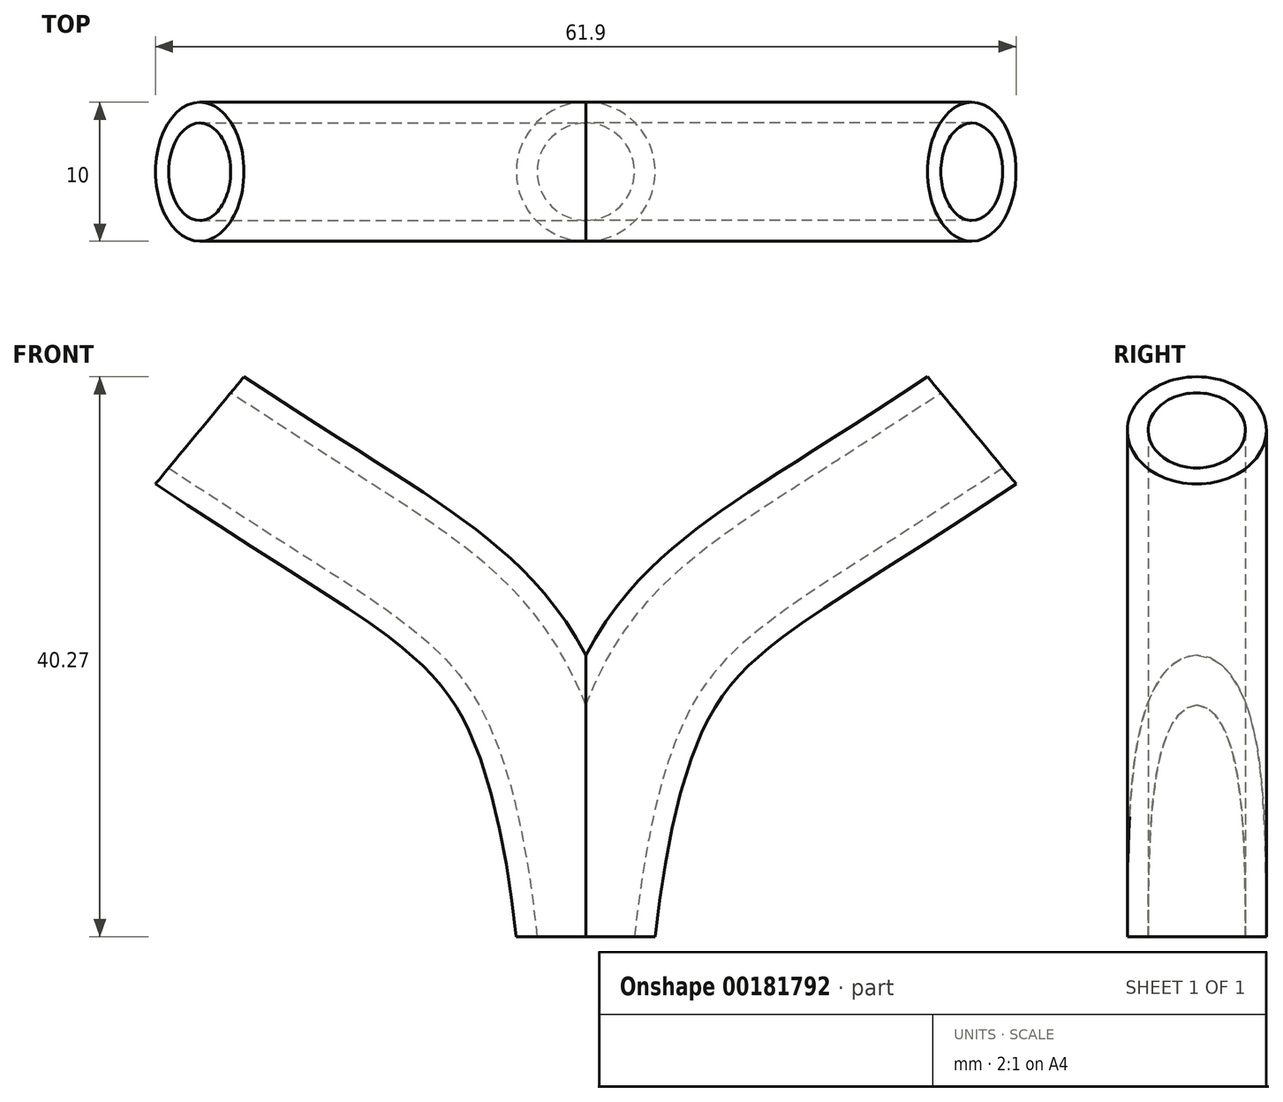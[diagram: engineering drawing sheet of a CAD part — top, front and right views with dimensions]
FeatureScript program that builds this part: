
annotation { "Feature Type Name" : "Feature", "Feature Type Description" : "" }
export const myFeature = defineFeature(function(context is Context, id is Id, definition is map)
    precondition{}
    {
        {
            var Q0;
            Q0=qCreatedBy(makeId("Front.planeOp"),FACE);
            var sketch = newSketch(context, id + "F0", { "sketchPlane" : qUnion([Q0])});
            skFitSpline(sketch, "E0", {"points": [v(0, 0) * mm, v(-8.85, 23.6) * mm, v(-27.77, 36.41) * mm], "startDerivative": vector(-9.3, 88.24) * mm, "endDerivative": vector(-66.03, 43.73) * mm});
            skSolve(sketch);
        }
        {
            var Q0;
            Q0=qCreatedBy(makeId("Top.planeOp"),FACE);
            var sketch = newSketch(context, id + "F1", { "sketchPlane" : qUnion([Q0])});
            skCircle(sketch, "E1", {"center": v(0, 0) * mm, "radius": 5 * mm});
            skCircle(sketch, "E2.0", {"center": v(0, 0) * mm, "radius": 3.5 * mm});
            skSolve(sketch);
        }
        {
            var Q0;
            Q0=makeQuery(id+"F1.imprint","IMPRINT",FACE,{"disambiguationData":[TD([[makeQuery(id+"F1.imprint","IMPRINT",EDGE,{"derivedFrom":sQuery(id+"F1.wireOp",EDGE,"E1")}),1.0]])]});
            var Q1;
            Q1=sQuery(id+"F0.wireOp",EDGE,"E0");
            sweep(context, id + "F2", {"profiles" : qUnion([Q0]), "path" : qUnion([Q1])});
        }
        {
            var Q0;
            Q0=qCreatedBy(makeId("Right.planeOp"),FACE);
            var sketch = newSketch(context, id + "F3", { "sketchPlane" : qUnion([Q0])});
            skLineSegment(sketch, "E3.bottom", {"start": v(-20.21, 23.68) * mm, "end": v(25, 23.68) * mm});
            skLineSegment(sketch, "E3.top", {"start": v(-20.21, -8.66) * mm, "end": v(25, -8.66) * mm});
            skLineSegment(sketch, "E3.left", {"start": v(-20.21, 23.68) * mm, "end": v(-20.21, -8.66) * mm});
            skLineSegment(sketch, "E3.right", {"start": v(25, 23.68) * mm, "end": v(25, -8.66) * mm});
            skSolve(sketch);
        }
        {
            var Q0;
            Q0 = qSketchRegion(id + "F3", true);
            extrude(context, id + "F4", {"entities" : qUnion([Q0]), "operationType" : NewBodyOperationType.REMOVE, "depth" : 5 * mm});
        }
        {
            var Q0;
            Q0=makeQuery(id+"F2.opSweep","SWEPT_BODY",BODY,{"disambiguationData":[OSD([sQuery(id+"F0.wireOp",EDGE,"E0"),sQuery(id+"F1.wireOp",EDGE,"E1"),sQuery(id+"F1.wireOp",EDGE,"E2.0")])]});
            var Q1;
            Q1=sQuery(id+"F1.wireOp",EDGE,"E2.0");
            circularPattern(context, id + "F5", {"entities" : qUnion([Q0]), "axis" : qUnion([Q1]), "angle" : 180 * degree, "instanceCount" : 2});
        }
    });
